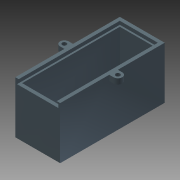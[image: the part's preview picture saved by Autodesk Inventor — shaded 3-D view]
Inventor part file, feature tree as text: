
AUTODESK INVENTOR PART (.ipt)
format: ipt  version: 2015 (Build 190159000, 159)  size: 210,432 bytes
history: native  units: mm
features: extrude x6, sketch x4, projected_geometry x4, plane x2, hole x1, other x1, pattern_circular x1, mirror x1
ambient origin geometry x8: Origin, YZ Plane, XZ Plane, XY Plane, X Axis, Y Axis, Z Axis, Center Point
bodies: Solid1 (feature_tree)
feature tree (20):
  sketch  "Sketch1"  dims[d0=29.85mm d1=8.0mm]
  extrude  "Extrusion1"  Depth=8.0mm
  extrude  "Extrusion2"  Depth=35.0mm
  sketch  "Sketch2"  dims[d2=40.0mm d3=35.0mm]
  extrude  "Extrusion3"  Depth=3.175mm
  extrude  "Extrusion4"  Depth=3.175mm
  sketch  "Sketch3"  dims[d4=3.175mm d5=3.175mm d6=3.175mm]
  extrude  "Extrusion5"  Depth=1.5875mm
  hole  "Hole1"  [1 undecoded]
  plane  "Work Plane1"
  plane  "Work Plane2"
  other  "Work Axis1"
  pattern_circular  "Circular Pattern1"  Count=9  [1 undecoded]
  extrude  "Extrusion6"  Depth=3.175mm TaperAngle=0.0deg
  mirror  "Mirror1"
  projected_geometry  "Projected Loop1"
  projected_geometry  "Projected Loop2"
  sketch  "Sketch4"  dims[d7=3.175mm d10=3.175mm d11=1.5875mm d12=1.5875mm d13=90.0mm d14=0.0mm d15=3.175mm d16=0.0mm d17=3.175mm d18=0.0mm d19=1.5875mm d20=0.0mm d21=1.03mm d22=19.5mm d23=25.5mm d24=1.5875mm d25=0.0mm d26=2.0mm d27=6.0mm d28=4.0mm d29=2.0mm d30=90.0deg d31=8.0mm d32=20.594885mm d33=90.0deg d34=90.0deg d35=80.0mm d36=360.0deg d38=4.0mm d39=4.0mm d40=2.0mm d41=5.0mm d42=0.0mm]
  projected_geometry  "Projected Loop3"
  projected_geometry  "Projected Loop4"
note: 2 required parameter values undecoded (feature->parameter linkage not recoverable at this tier; creation-order binding heuristic only, values carry confidence <= 0.55)
